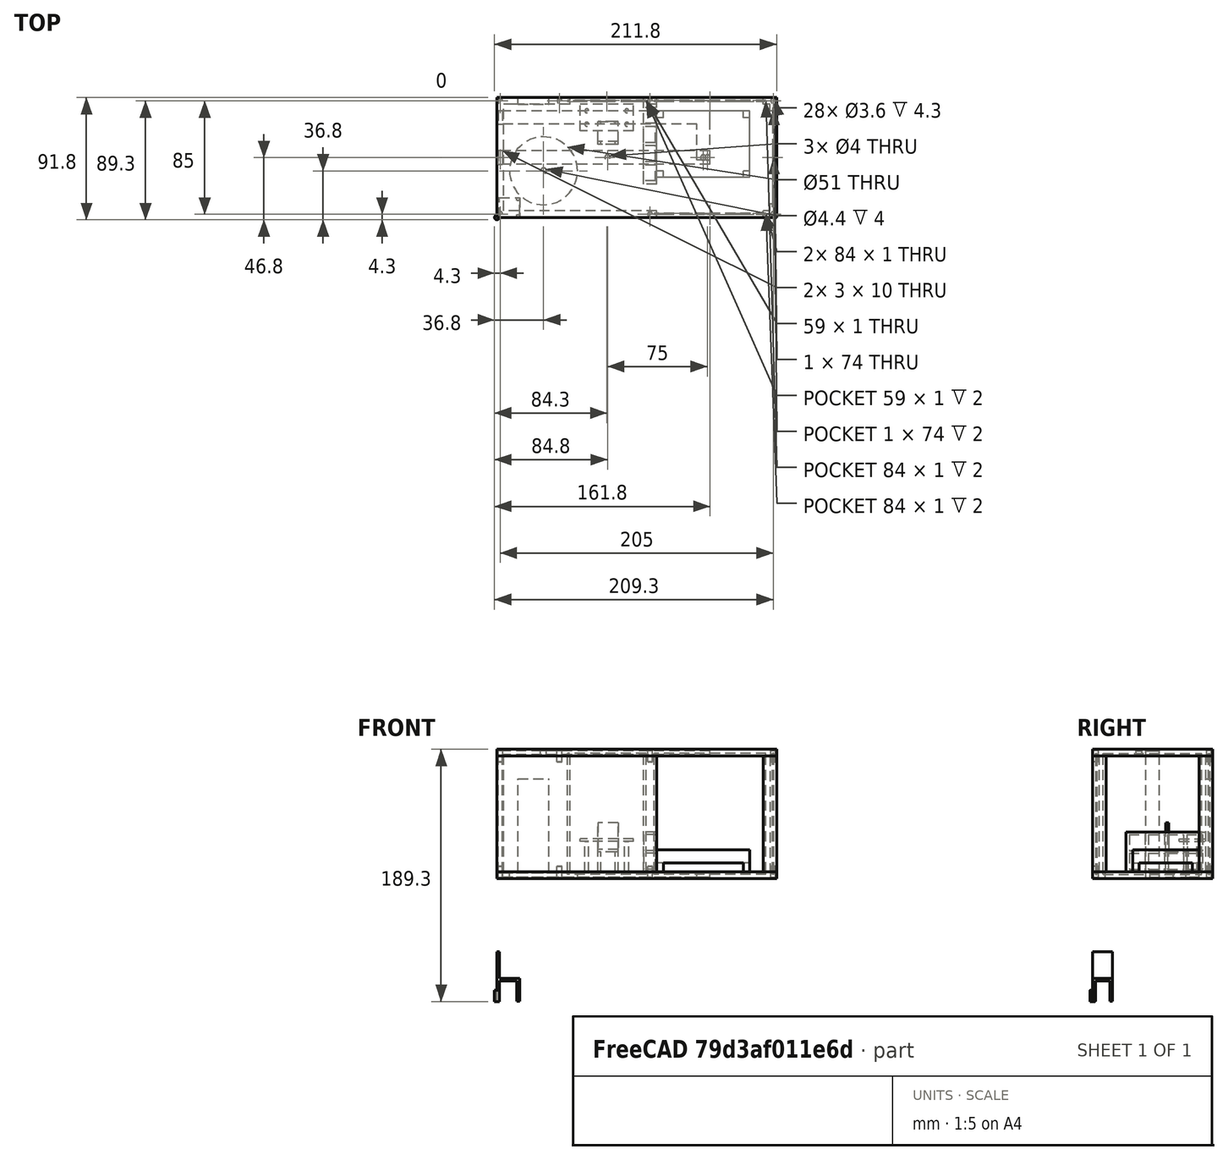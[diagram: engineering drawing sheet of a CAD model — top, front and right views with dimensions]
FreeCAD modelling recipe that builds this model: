
FCSTD DOCUMENT  (FreeCAD 0.15R4671 (Git))
Label: Dormitorio
License: CreativeCommons Attribution-ShareAlike
LicenseURL: http://creativecommons.org/licenses/by-sa/4.0/
objects: Part::Box×26, Part::Cut×21, Part::Feature×19, Part::MultiFuse×10, Part::Cylinder×5, Part::FeaturePython×4, App::DocumentObjectGroup×2, Part::Offset×1
note: 86 computed .brp shape members not serialized (recipe doc carries the construction recipe); baked Part::Feature solids carry a one-line shape summary decoded from their .brp

FEATURE [Part::Box] Box  label="suelo macizo conteiner 20""
  Height = 5
  Length = 90
  Placement = pos=(0,0,-5) rot=(0,0,1;0rad)
  Width = 210
FEATURE [Part::Box] Box001  label="Techo macizo conteiner 20""
  Height = 5
  Length = 90
  Placement = pos=(0,0,87) rot=(0,0,1;0rad)
  Width = 210
FEATURE [Part::Box] Box002  label="larguero vertical esquina 1_1"
  Height = 87
  Length = 10
  Width = 5
FEATURE [Part::Box] Box003  label="larguero vertical esquina 1_2"
  Height = 87
  Length = 5
  Width = 10
FEATURE [Part::MultiFuse] Fusion  label="Larguero esquina 1 dormitorio"
  Shapes = -> [Box002,Box003]
FEATURE [Part::Box] Box004  label="larguero vertical esquina 2_1"
  Height = 87
  Length = 10
  Placement = pos=(80,0,0) rot=(0,0,1;0rad)
  Width = 5
FEATURE [Part::Box] Box005  label="larguero vertical esquina 2_2"
  Height = 87
  Length = 5
  Placement = pos=(85,0,0) rot=(0,0,1;0rad)
  Width = 10
FEATURE [Part::MultiFuse] Fusion001  label="Larguero esquina 2 dormitorio"
  Shapes = -> [Box004,Box005]
FEATURE [Part::Box] Box006  label="Columna media master dormitorio"
  Height = 87
  Length = 5
  Placement = pos=(85,90,0) rot=(0,0,1;0rad)
  Width = 10
FEATURE [Part::Cylinder] Cylinder  label="hueco escalera caracol"
  Angle = 360
  Height = 10
  Placement = pos=(35,175,-7) rot=(0,0,1;0rad)
  Radius = 25.5
FEATURE [Part::Box] Box007  label="Tabique macizo dormitorio para puerta solarium"
  Height = 87
  Length = 5
  Placement = pos=(85,155,0) rot=(0,0,1;0rad)
  Width = 55
FEATURE [Part::Box] Box008  label="Tabique trasero dormitorio"
  Height = 87
  Length = 80
  Placement = pos=(5,205,0) rot=(0,0,1;0rad)
  Width = 5
FEATURE [Part::Box] Box009  label="Tabique largo dormitorio"
  Height = 87
  Length = 5
  Placement = pos=(0,90,0) rot=(0,0,1;0rad)
  Width = 120
FEATURE [Part::MultiFuse] Fusion002  label="Pared esquinazo dormitorio"
  Shapes = -> [Box007,Box008,Box009]
FEATURE [Part::Box] Box010  label="Hueco puerta paso solarium"
  Height = 70
  Length = 10
  Placement = pos=(83,170.833,0) rot=(0,0,1;0rad)
  Width = 23.3333
FEATURE [Part::Cut] Cut  label="Pared esquinazo dormitorio + puerta solarium"
  Base = -> Fusion002
  Tool = -> Box010
FEATURE [Part::Cut] Cut001  label="suelo con hueco escalera caracol"
  Base = -> Box
  Tool = -> Cylinder
FEATURE [Part::Box] Box011  label="Base cama  150"
  Height = 10
  Length = 50
  Placement = pos=(30,20,6.66667) rot=(0,0,1;0rad)
  Width = 70
FEATURE [Part::Box] Box012  label="master pata cama "
  Height = 6.66667
  Length = 5
  Placement = pos=(30,20,0) rot=(0,0,1;0rad)
  Width = 5
FEATURE [Part::FeaturePython] Array  label="Patas de la cama"  # Draft array (typed FeaturePython)
  Angle = 360
  ArrayType = 0
  Axis = (0,0,1)
  Base = -> Box012
  Center = (0,0,0)
  Fuse = false
  IntervalAxis = (0,0,0)
  IntervalX = (45,0,0)
  IntervalY = (0,65,0)
  IntervalZ = (0,0,0)
  NumberPolar = 1
  NumberX = 2
  NumberY = 2
  NumberZ = 1
FEATURE [Part::MultiFuse] Fusion003  label="Cama 150"
  Placement = pos=(210,0,97) rot=(0,0,1;1.5708rad)
  Shapes = -> [Box011,Array]
FEATURE [Part::Box] Box014  label="Libreria baja dormitorio maciza"
  Height = 30
  Length = 60
  Placement = pos=(25,90,0) rot=(0,0,1;0rad)
  Width = 10
FEATURE [Part::Box] Box015  label="master vaciado libreria baja"
  Height = 12
  Length = 12
  Width = 10
FEATURE [Part::FeaturePython] Array001  label="Matriz huecos libreria baja"  # Draft array (typed FeaturePython)
  Angle = 360
  ArrayType = 0
  Axis = (0,0,1)
  Base = -> Box015
  Center = (0,0,0)
  Fuse = false
  IntervalAxis = (0,0,0)
  IntervalX = (14.4,0,0)
  IntervalY = (0,1,0)
  IntervalZ = (0,0,14)
  NumberPolar = 1
  NumberX = 4
  NumberY = 1
  NumberZ = 2
  Placement = pos=(27.4,91,2) rot=(0,0,1;0rad)
FEATURE [Part::Cut] Cut002  label="Libreria baja dormitorio"
  Base = -> Box014
  Placement = pos=(210,0,97) rot=(0,0,1;1.5708rad)
  Tool = -> Array001
FEATURE [Part::Box] Box016  label="Tablero mesa escritorio"
  Height = 1.66667
  Length = 20
  Placement = pos=(65,107.5,23) rot=(0,0,1;0rad)
  Width = 40
FEATURE [Part::Cylinder] Cylinder001  label="Master pata mesa escritorio"
  Angle = 360
  Height = 23
  Placement = pos=(70,112.5,0) rot=(0,0,1;0rad)
  Radius = 1.5
FEATURE [Part::FeaturePython] Array002  label="Matriz 4 patas mesa escritorio"  # Draft array (typed FeaturePython)
  Angle = 360
  ArrayType = 0
  Axis = (0,0,1)
  Base = -> Cylinder001
  Center = (0,0,0)
  Fuse = false
  IntervalAxis = (0,0,0)
  IntervalX = (10,0,0)
  IntervalY = (0,30,0)
  IntervalZ = (0,0,0)
  NumberPolar = 1
  NumberX = 2
  NumberY = 2
  NumberZ = 1
FEATURE [Part::Box] Box017  label="Exterior silla"
  Height = 22
  Length = 17
  Width = 15
FEATURE [Part::Box] Box018  label="Vaciado respaldo silla"
  Height = 25
  Length = 25
  Placement = pos=(2,-2,2) rot=(0,0,1;0rad)
  Width = 20
FEATURE [Part::Cut] Cut003  label="Respaldo + Base silla"
  Base = -> Box017
  Placement = pos=(0,0,15) rot=(0,0,1;0rad)
  Tool = -> Box018
FEATURE [Part::MultiFuse] Fusion004  label="Mesa escritorio"
  Placement = pos=(210,0,97) rot=(0,0,1;1.5708rad)
  Shapes = -> [Box016,Array002]
FEATURE [Part::Box] Box019  label="Master pata silla"
  Height = 15
  Length = 2
  Width = 2
FEATURE [Part::FeaturePython] Array003  label="Matriz 4 patas silla"  # Draft array (typed FeaturePython)
  Angle = 360
  ArrayType = 0
  Axis = (0,0,1)
  Base = -> Box019
  Center = (0,0,0)
  Fuse = false
  IntervalAxis = (0,0,0)
  IntervalX = (15,0,0)
  IntervalY = (0,13,0)
  IntervalZ = (0,0,0)
  NumberPolar = 1
  NumberX = 2
  NumberY = 2
  NumberZ = 1
FEATURE [Part::MultiFuse] Fusion005  label="Silla master"
  Shapes = -> [Cut003,Array003]
FEATURE [Part::Feature] Fusion005001  label="Silla dormitorio"
  Placement = pos=(91,55,97) rot=(0,0,1;1.5708rad)
  shape: bbox 15 x 17 x 37 mm, 20 faces (baked)
FEATURE [Part::Cylinder] Cylinder002  label="conector master"
  Angle = 360
  Height = 8
  Radius = 1.5
FEATURE [Part::Offset] Offset  label="Offset conector master"
  Fill = false
  Intersection = false
  Join = 2
  Mode = 1
  SelfIntersection = false
  Source = -> Cylinder002
  Value = 0.3
FEATURE [Part::Feature] Offset001  label="Vaciado conector 1"
  Placement = pos=(2.5,2.5,-4) rot=(0,0,1;0rad)
  shape: bbox 3.602 x 3.602 x 8.602 mm, 3 faces (baked)
FEATURE [Part::Feature] Offset002  label="Vaciado conector 2"
  Placement = pos=(87.5,2.5,-4) rot=(0,0,1;0rad)
  shape: bbox 3.602 x 3.602 x 8.602 mm, 3 faces (baked)
FEATURE [Part::Feature] Offset001001  label="Vaciado conector 3"
  Placement = pos=(2.5,2.5,83) rot=(0,0,1;0rad)
  shape: bbox 3.602 x 3.602 x 8.602 mm, 3 faces (baked)
FEATURE [Part::Feature] Offset002001  label="Vaciado conector 4"
  Placement = pos=(87.5,2.5,83) rot=(0,0,1;0rad)
  shape: bbox 3.602 x 3.602 x 8.602 mm, 3 faces (baked)
FEATURE [Part::Feature] Offset002002  label="Vaciado conector 5"
  Placement = pos=(87.5,95,-4) rot=(0,0,1;0rad)
  shape: bbox 3.602 x 3.602 x 8.602 mm, 3 faces (baked)
FEATURE [Part::Feature] Offset002002001  label="Vaciado conector 6"
  Placement = pos=(87.5,95,83) rot=(0,0,1;0rad)
  shape: bbox 3.602 x 3.602 x 8.602 mm, 3 faces (baked)
FEATURE [Part::Feature] Offset002002002  label="Vaciado conector 7"
  Placement = pos=(87.5,163,-4) rot=(0,0,1;0rad)
  shape: bbox 3.602 x 3.602 x 8.602 mm, 3 faces (baked)
FEATURE [Part::Feature] Offset002002002001  label="Vaciado conector 8"
  Placement = pos=(87.5,163,83) rot=(0,0,1;0rad)
  shape: bbox 3.602 x 3.602 x 8.602 mm, 3 faces (baked)
FEATURE [Part::Feature] Offset002002002002  label="Vaciado conector 9"
  Placement = pos=(87.5,207.5,-4) rot=(0,0,1;0rad)
  shape: bbox 3.602 x 3.602 x 8.602 mm, 3 faces (baked)
FEATURE [Part::Feature] Offset002002002002001  label="Vaciado conector 10"
  Placement = pos=(87.5,207.5,83) rot=(0,0,1;0rad)
  shape: bbox 3.602 x 3.602 x 8.602 mm, 3 faces (baked)
FEATURE [Part::Feature] Offset001002  label="Vaciado conector 11"
  Placement = pos=(2.5,207.5,83) rot=(0,0,1;0rad)
  shape: bbox 3.602 x 3.602 x 8.602 mm, 3 faces (baked)
FEATURE [Part::Feature] Offset001002001  label="Vaciado conector 12"
  Placement = pos=(2.5,207.5,-4) rot=(0,0,1;0rad)
  shape: bbox 3.602 x 3.602 x 8.602 mm, 3 faces (baked)
FEATURE [Part::Feature] Offset001002002  label="Vaciado conector 13"
  Placement = pos=(2.5,95,-4) rot=(0,0,1;0rad)
  shape: bbox 3.602 x 3.602 x 8.602 mm, 3 faces (baked)
FEATURE [Part::Feature] Offset001002002001  label="Vaciado conector 14"
  Placement = pos=(2.5,95,83) rot=(0,0,1;0rad)
  shape: bbox 3.602 x 3.602 x 8.602 mm, 3 faces (baked)
FEATURE [Part::Box] Box020  label="cristal frontal"
  Height = 91
  Length = 74
  Placement = pos=(208,8,95) rot=(0,0,1;1.5708rad)
  Width = 1
FEATURE [Part::Box] Box021  label="cristal lateral izquierdo"
  Height = 91
  Length = 1
  Placement = pos=(202,2,95) rot=(0,0,1;1.5708rad)
  Width = 84
FEATURE [Part::Feature] Box021001  label="cristal lateral derecho cama"
  Placement = pos=(202,87,95) rot=(0,0,1;1.5708rad)
  shape: bbox 84 x 1 x 91 mm, 6 faces (baked)
FEATURE [Part::Box] Box021002  label="cristal escritorio"
  Height = 91
  Length = 1
  Placement = pos=(112,87,95) rot=(0,0,1;1.5708rad)
  Width = 59
FEATURE [Part::MultiFuse] Fusion005002  label="Union Cristales y conectores"
  Shapes = -> [Box020,Box021,Box021001,Box021002,Offset001002002001,Offset001002002,Offset001002001,Offset001002,Offset002002002002001,Offset002002002002,Offset002002002001,Offset002002002,Offset002002001,Offset002002,Offset002001,Offset001001,Offset002,Offset001]
FEATURE [Part::Cut] Cut004  label="Larguero dormitorio esquina 1 con vaciados sin hueco cristales"
  Base = -> Fusion
  Placement = pos=(210,0,97) rot=(0,0,1;1.5708rad)
  Tool = -> Fusion005002
FEATURE [Part::Cut] Cut005  label="Larguero dormitorio esquina 2 con vaciados sin hueco cristales"
  Base = -> Fusion001
  Placement = pos=(210,0,97) rot=(0,0,1;1.5708rad)
  Tool = -> Fusion005002
FEATURE [Part::Cut] Cut006  label="Techo container con vaciados conectores y cristales"
  Base = -> Box001
  Tool = -> Fusion005002
FEATURE [Part::Cut] Cut007  label="Suelo con vaciados cristales y conectores"
  Base = -> Cut001
  Tool = -> Fusion005002
FEATURE [Part::Cut] Cut008  label="Columna media dormitorio con vaciados sin hueco cristales"
  Base = -> Box006
  Placement = pos=(210,0,97) rot=(0,0,1;1.5708rad)
  Tool = -> Fusion005002
FEATURE [Part::Cut] Cut009  label="Pared esquinazo dormitorio con vaciados"
  Base = -> Cut
  Tool = -> Fusion005002
FEATURE [Part::Box] Box021003  label="Roza cables techo"
  Height = 3
  Length = 10
  Placement = pos=(40,50,88) rot=(0,0,1;0rad)
  Width = 159
FEATURE [Part::Cylinder] Cylinder003  label="Hueco Techo Led cama"
  Angle = 360
  Height = 10
  Placement = pos=(45,52,81) rot=(0,0,1;0rad)
  Radius = 2
FEATURE [Part::Feature] Cylinder003001  label="Hueco Techo Led escritorio"
  Placement = pos=(45,127,81) rot=(0,0,1;0rad)
  shape: bbox 4 x 4 x 10 mm, 3 faces (baked)
FEATURE [Part::Box] Box021004  label="Roza muro vertical "
  Height = 101
  Length = 10
  Placement = pos=(40,206,-10) rot=(0,0,1;0rad)
  Width = 3
FEATURE [Part::Feature] Box021003001  label="Roza cables zona porche"
  Placement = pos=(70,50,-4) rot=(0,0,1;0rad)
  shape: bbox 10 x 159 x 3 mm, 6 faces (baked)
FEATURE [Part::Box] Box021003002  label="Roza cables porche angular"
  Height = 3
  Length = 30
  Placement = pos=(43,50,-4) rot=(0,0,1;0rad)
  Width = 10
FEATURE [Part::Feature] Cylinder003002  label="Hueco Techo Led Zona Porche"
  Placement = pos=(45,55,-11) rot=(0,0,1;0rad)
  shape: bbox 4 x 4 x 10 mm, 3 faces (baked)
FEATURE [Part::Box] Box021003003  label="Roza salida cables al techo modulo central"
  Height = 10
  Length = 10
  Placement = pos=(70,206,-11) rot=(0,0,1;0rad)
  Width = 3
FEATURE [Part::MultiFuse] Fusion005003  label="Roza techo dormitorio"
  Shapes = -> [Box021003,Cylinder003,Cylinder003001,Box021004]
FEATURE [Part::MultiFuse] Fusion005004  label="Roza luz zona porche exterior"
  Shapes = -> [Box021003001,Box021003002,Cylinder003002,Box021003003]
FEATURE [Part::Cut] Cut010  label="Techo dormitorio sin encastre barra escalera"
  Base = -> Cut006
  Placement = pos=(210,0,97) rot=(0,0,1;1.5708rad)
  Tool = -> Fusion005003
FEATURE [Part::Cut] Cut011  label="Paredes Esquinazo Dormitorio sin hueco cristales"
  Base = -> Cut009
  Placement = pos=(210,0,97) rot=(0,0,1;1.5708rad)
  Tool = -> Fusion005003
FEATURE [Part::Cut] Cut012  label="Suelo - salida cables techo dormitorio"
  Base = -> Cut007
  Tool = -> Fusion005003
FEATURE [Part::Cut] Cut013  label="Suelo Dormitorio y Techo Zona Porche sin hueco cristales"
  Base = -> Cut012
  Placement = pos=(210,0,97) rot=(0,0,1;1.5708rad)
  Tool = -> Fusion005004
FEATURE [App::DocumentObjectGroup] Grupo  label="Mobiliario dormitorio"
  Group = -> [Fusion003,Cut002,Fusion004,Fusion005001,Fusion005]
FEATURE [Part::Cylinder] Cylinder003003  label="Hueco encastre superior barra escalera"
  Angle = 360
  Height = 10
  Placement = pos=(35,35,178) rot=(0,0,1;0rad)
  Radius = 2.2
FEATURE [Part::Cut] Cut014  label="Techo Dormitorio sin huecos cristales"
  Base = -> Cut010
  Tool = -> Cylinder003003
FEATURE [Part::MultiFuse] Fusion005005  label="cristales"
  Shapes = -> [Box020,Box021,Box021001,Box021002]
FEATURE [Part::Cut] Cut015  label="Techo dormitorio"
  Base = -> Cut014
  Tool = -> Fusion005005
FEATURE [Part::Cut] Cut016  label="Larguero dormitorio esquina 1 con vaciados"
  Base = -> Cut004
  Tool = -> Fusion005005
FEATURE [Part::Cut] Cut017  label="Larguero dormitorio esquina 2 con vaciados"
  Base = -> Cut005
  Tool = -> Fusion005005
FEATURE [Part::Cut] Cut018  label="Columna media dormitorio con vaciados"
  Base = -> Cut008
  Tool = -> Fusion005005
FEATURE [Part::Cut] Cut019  label="Pared Esquinazo Dormitorio"
  Base = -> Cut011
  Tool = -> Fusion005005
FEATURE [Part::Cut] Cut020  label="Suelo Dormitorio y Techo Zona Porche"
  Base = -> Cut013
  Tool = -> Fusion005005
FEATURE [App::DocumentObjectGroup] Grupo001  label="Elementos constructivos Dormitorio"
  Group = -> [Offset,Cut015,Cut016,Cut017,Cut018,Cut019,Cut020]
